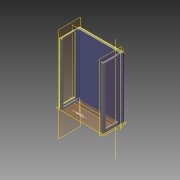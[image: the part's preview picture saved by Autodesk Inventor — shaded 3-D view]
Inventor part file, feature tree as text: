
AUTODESK INVENTOR PART (.ipt)
format: ipt  version: 2015 (Build 190159000, 159)  size: 176,128 bytes
history: native  units: mm
features: sketch x7, projected_geometry x5, extrude x4, plane x1
ambient origin geometry x8: Origin, YZ Plane, XZ Plane, XY Plane, X Axis, Y Axis, Z Axis, Center Point
bodies: Solid1 (feature_tree)
feature tree (17):
  extrude  "Extrusion1"  Depth=24.0mm
  extrude  "Extrusion2"  Depth=2.0mm
  extrude  "Extrusion3"  Depth=3.0mm TaperAngle=0.0deg
  extrude  "Extrusion4"  Depth=2.0mm
  sketch  "Sketch9"  dims[d13=2.0mm]
  plane  "Work Plane1"
  sketch  "Sketch10"  dims[d14=2.0mm]
  sketch  "Sketch11"  dims[d15=2.0mm d16=2.0mm d17=0.0mm d36=0.0mm]
  sketch  "Sketch1"  dims[d0=2.0mm d1=24.0mm]
  sketch  "Sketch3"  dims[d2=2.0mm d3=32.0mm]
  projected_geometry  "Projected Loop1"
  projected_geometry  "Projected Loop2"
  sketch  "Sketch4"  dims[d4=94.2mm d5=0.0mm d6=3.0mm d7=0.0mm]
  projected_geometry  "Projected Loop3"
  sketch  "Sketch7"  dims[d8=2.0mm d9=0.0mm d12=2.0mm]
  projected_geometry  "Projected Loop5"
  projected_geometry  "Projected Loop6"
